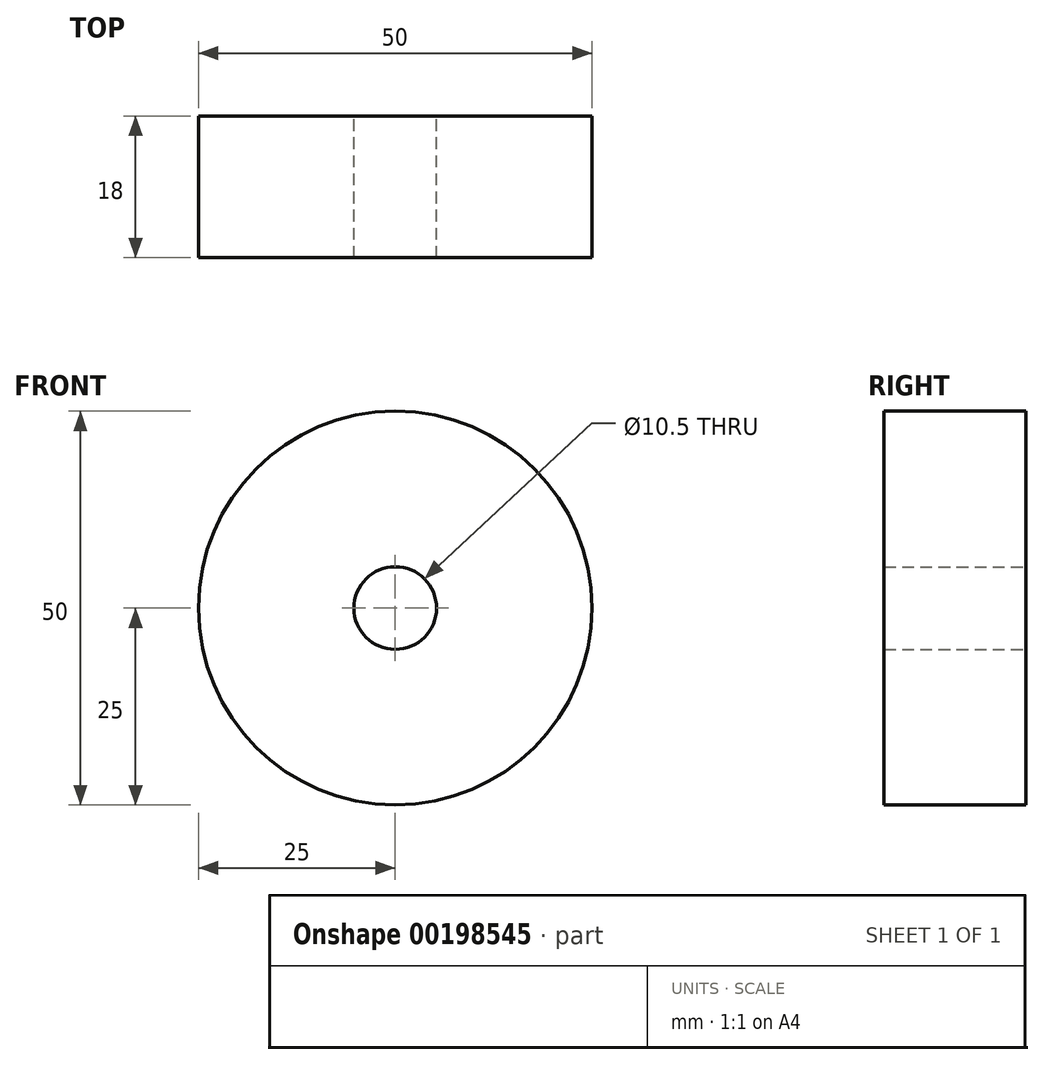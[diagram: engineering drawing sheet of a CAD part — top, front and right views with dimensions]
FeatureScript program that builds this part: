
annotation { "Feature Type Name" : "Feature", "Feature Type Description" : "" }
export const myFeature = defineFeature(function(context is Context, id is Id, definition is map)
    precondition{}
    {
        {
            var Q0;
            Q0=qCreatedBy(makeId("Front.planeOp"),FACE);
            var sketch = newSketch(context, id + "F0", { "sketchPlane" : qUnion([Q0])});
            skCircle(sketch, "E0", {"center": v(0, 0) * mm, "radius": 25 * mm});
            skCircle(sketch, "E1", {"center": v(0, 0) * mm, "radius": 5.25 * mm});
            skSolve(sketch);
        }
        {
            var Q0;
            Q0=makeQuery(id+"F0.imprint","IMPRINT",FACE,{"disambiguationData":[TD([[makeQuery(id+"F0.imprint","IMPRINT",EDGE,{"derivedFrom":sQuery(id+"F0.wireOp",EDGE,"E0")}),1.0]])]});
            extrude(context, id + "F1", {"entities" : qUnion([Q0]), "depth" : 18 * mm});
        }
    });
